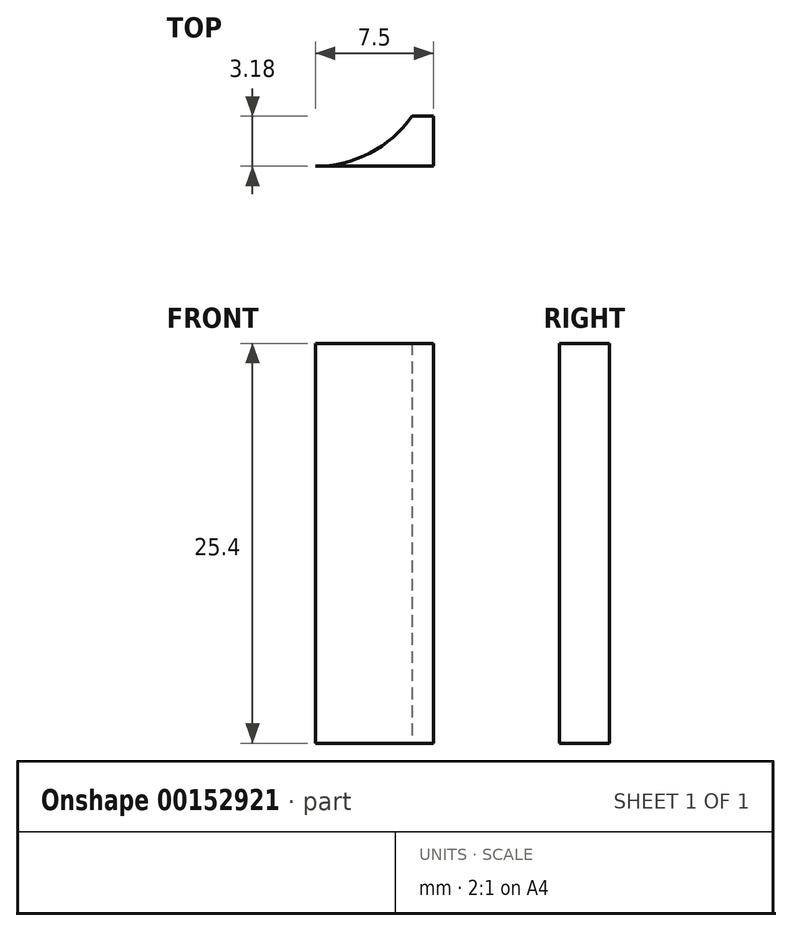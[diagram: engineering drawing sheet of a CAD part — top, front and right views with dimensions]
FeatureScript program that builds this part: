
annotation { "Feature Type Name" : "Feature", "Feature Type Description" : "" }
export const myFeature = defineFeature(function(context is Context, id is Id, definition is map)
    precondition{}
    {
        {
            var Q0;
            Q0=qCreatedBy(makeId("Top.planeOp"),FACE);
            var sketch = newSketch(context, id + "F0", { "sketchPlane" : qUnion([Q0])});
            skLineSegment(sketch, "E0.bottom", {"start": v(0, 0) * mm, "end": v(7.5, 0) * mm});
            skLineSegment(sketch, "E0.right", {"start": v(7.5, 0) * mm, "end": v(7.5, 3.18) * mm});
            skLineSegment(sketch, "E1", {"start": v(7.5, 3.18) * mm, "end": v(6.13, 3.18) * mm});
            skArc(sketch, "E2", {"start": v(0, 0) * mm, "mid": v(3.45, 0.84) * mm, "end": v(6.13, 3.18) * mm});
            skSolve(sketch);
        }
        {
            var Q0;
            Q0 = qSketchRegion(id + "F0", true);
            extrude(context, id + "F1", {"entities" : qUnion([Q0]), "depth" : 25.4 * mm});
        }
    });
